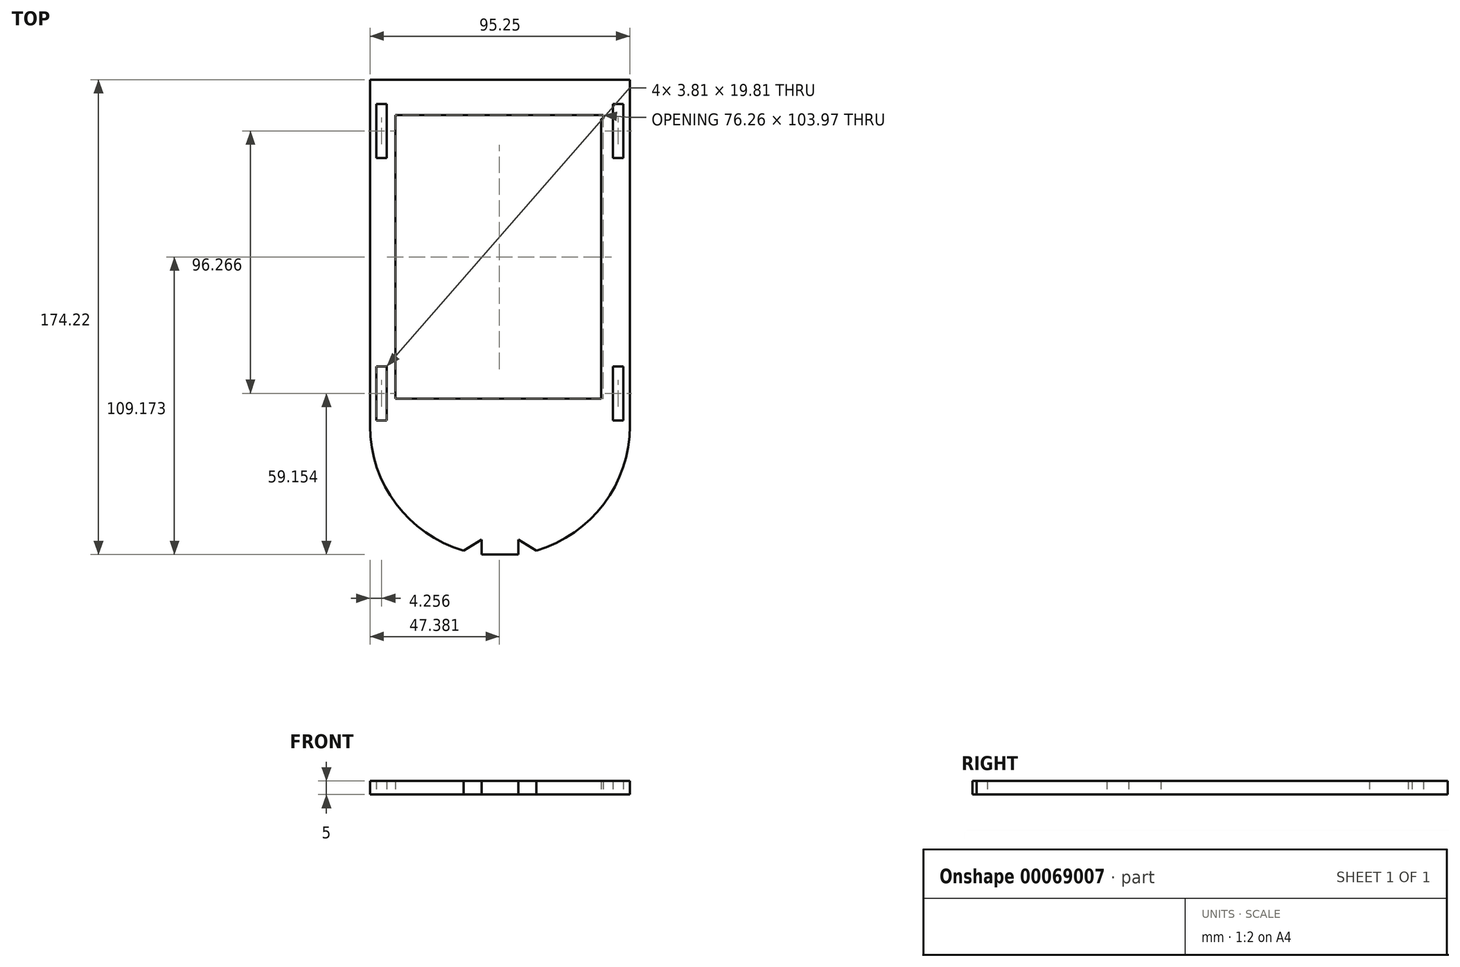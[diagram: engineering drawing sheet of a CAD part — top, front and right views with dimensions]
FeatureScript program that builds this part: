
annotation { "Feature Type Name" : "Feature", "Feature Type Description" : "" }
export const myFeature = defineFeature(function(context is Context, id is Id, definition is map)
    precondition{}
    {
        {
            var Q0;
            Q0=qCreatedBy(makeId("Top.planeOp"),FACE);
            var sketch = newSketch(context, id + "F0", { "sketchPlane" : qUnion([Q0])});
            skLineSegment(sketch, "E0.bottom", {"start": v(-47.36, 43.06) * mm, "end": v(47.9, 43.06) * mm});
            skLineSegment(sketch, "E0.left", {"start": v(-47.36, 43.06) * mm, "end": v(-47.36, -83.94) * mm});
            skLineSegment(sketch, "E0.right", {"start": v(47.9, 43.06) * mm, "end": v(47.9, -83.94) * mm});
            skLineSegment(sketch, "E1.bottom", {"start": v(-45, 34.17) * mm, "end": v(-41.2, 34.17) * mm});
            skLineSegment(sketch, "E1.top", {"start": v(-45, 14.35) * mm, "end": v(-41.2, 14.35) * mm});
            skLineSegment(sketch, "E1.left", {"start": v(-45, 34.17) * mm, "end": v(-45, 14.35) * mm});
            skLineSegment(sketch, "E1.right", {"start": v(-41.2, 34.17) * mm, "end": v(-41.2, 14.35) * mm});
            skLineSegment(sketch, "E2.bottom", {"start": v(-41.2, -81.91) * mm, "end": v(-45, -81.91) * mm});
            skLineSegment(sketch, "E2.top", {"start": v(-41.2, -62.1) * mm, "end": v(-45, -62.1) * mm});
            skLineSegment(sketch, "E2.left", {"start": v(-41.2, -81.91) * mm, "end": v(-41.2, -62.1) * mm});
            skLineSegment(sketch, "E2.right", {"start": v(-45, -81.91) * mm, "end": v(-45, -62.1) * mm});
            skLineSegment(sketch, "E3", {"start": v(-13.07, -129.66) * mm, "end": v(-6.5, -125.7) * mm});
            skLineSegment(sketch, "E4", {"start": v(7.03, -125.7) * mm, "end": v(13.6, -129.66) * mm});
            skArc(sketch, "E5", {"start": v(-47.36, -83.94) * mm, "mid": v(-37.83, -112.52) * mm, "end": v(-13.07, -129.66) * mm});
            skArc(sketch, "E6", {"start": v(13.6, -129.66) * mm, "mid": v(38.37, -112.52) * mm, "end": v(47.9, -83.94) * mm});
            skLineSegment(sketch, "E7", {"start": v(-6.5, -125.7) * mm, "end": v(-6.5, -131.16) * mm});
            skLineSegment(sketch, "E8", {"start": v(7.03, -125.7) * mm, "end": v(7.03, -131.16) * mm});
            skLineSegment(sketch, "E9", {"start": v(-6.5, -131.16) * mm, "end": v(7.03, -131.16) * mm});
            skLineSegment(sketch, "E10.bottom", {"start": v(45.53, -62.1) * mm, "end": v(41.72, -62.1) * mm});
            skLineSegment(sketch, "E10.top", {"start": v(45.53, -81.91) * mm, "end": v(41.72, -81.91) * mm});
            skLineSegment(sketch, "E10.left", {"start": v(45.53, -62.1) * mm, "end": v(45.53, -81.91) * mm});
            skLineSegment(sketch, "E10.right", {"start": v(41.72, -62.1) * mm, "end": v(41.72, -81.91) * mm});
            skLineSegment(sketch, "E11.bottom", {"start": v(45.53, 34.17) * mm, "end": v(41.72, 34.17) * mm});
            skLineSegment(sketch, "E11.top", {"start": v(45.53, 14.35) * mm, "end": v(41.72, 14.35) * mm});
            skLineSegment(sketch, "E11.left", {"start": v(45.53, 34.17) * mm, "end": v(45.53, 14.35) * mm});
            skLineSegment(sketch, "E11.right", {"start": v(41.72, 34.17) * mm, "end": v(41.72, 14.35) * mm});
            skLineSegment(sketch, "E12.bottom", {"start": v(-38.1, 30) * mm, "end": v(38.15, 30) * mm});
            skLineSegment(sketch, "E12.top", {"start": v(-38.1, 28.6) * mm, "end": v(38.15, 28.6) * mm});
            skLineSegment(sketch, "E12.left", {"start": v(-38.1, 30) * mm, "end": v(-38.1, 28.6) * mm});
            skLineSegment(sketch, "E12.right", {"start": v(38.15, 30) * mm, "end": v(38.15, 28.6) * mm});
            skLineSegment(sketch, "E13.bottom", {"start": v(38.15, 30) * mm, "end": v(-38.1, 30) * mm});
            skLineSegment(sketch, "E13.top", {"start": v(38.15, 28.6) * mm, "end": v(-38.1, 28.6) * mm});
            skLineSegment(sketch, "E14.bottom", {"start": v(-38.1, 28.6) * mm, "end": v(37.33, 28.6) * mm});
            skLineSegment(sketch, "E14.top", {"start": v(-38.1, -73.97) * mm, "end": v(37.33, -73.97) * mm});
            skLineSegment(sketch, "E14.left", {"start": v(-38.1, 28.6) * mm, "end": v(-38.1, -73.97) * mm});
            skLineSegment(sketch, "E14.right", {"start": v(37.33, 28.6) * mm, "end": v(37.33, -73.97) * mm});
            skSolve(sketch);
        }
        {
            var Q0;
            Q0=makeQuery(id+"F0.imprint","IMPRINT",FACE,{"disambiguationData":[TD([[makeQuery(id+"F0.imprint","IMPRINT",EDGE,{"derivedFrom":sQuery(id+"F0.wireOp",EDGE,"E0.bottom")}),-1.0]])]});
            extrude(context, id + "F1", {"entities" : qUnion([Q0]), "depth" : 5 * mm});
        }
    });
